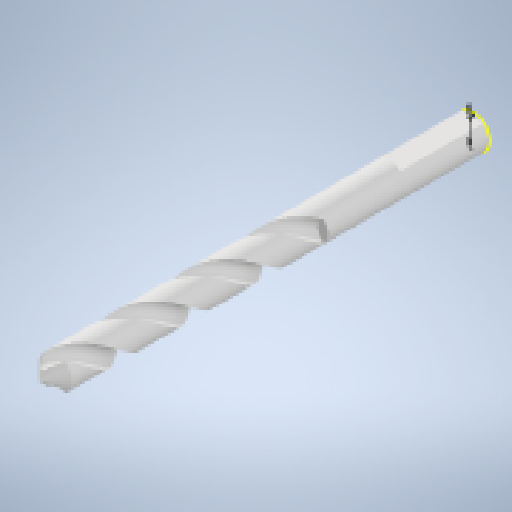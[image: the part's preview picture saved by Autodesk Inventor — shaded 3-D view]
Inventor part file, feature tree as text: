
AUTODESK INVENTOR PART (.ipt)
format: ipt  version: 2024.2 (Build 282272000, 272)  size: 218,624 bytes
history: native  units: in
note: dims shown in document units (in); Inventor stores cm internally (conversion verified against a paired STEP export)
features: sketch x1, other x1
ambient origin geometry x8: Origin, YZ Plane, XZ Plane, XY Plane, X Axis, Y Axis, Z Axis, Center Point
bodies: Solid1 (feature_tree)
feature tree (2):
  sketch  "Sketch1"  dims[d0=0.315in]
  other  "Cut-Extrude1"
